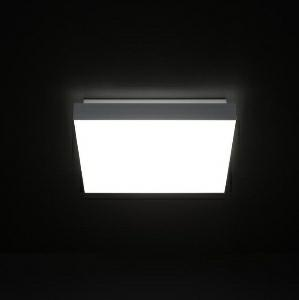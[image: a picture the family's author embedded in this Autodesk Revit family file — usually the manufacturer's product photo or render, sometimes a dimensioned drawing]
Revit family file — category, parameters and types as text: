
# Revit family: spectral_norea_norea-qa_625_5200_840_os_b266
name_source: partatom
category: Lighting Fixtures
revit_build: Autodesk Revit 2016 (Build: 20150220_1215(x64)
units: mm (PartAtom-declared; Revit-internal decimal feet)

## family parameters
Cut with Voids When Loaded = No
Host = Face
Light Source = No
Part Type = Normal
Room Calculation Point = No
Round Connector Dimension = Use Diameter
Shared = No

## types (1)
- SPECTRAL NOREA (1 x )
    Apparent Load = 0 VA
    Approval mark = CE
    CIE Flux Codes = 48 78 95 100 66
    Control Gear = Electronic transformer
    Default Elevation = 1800 mm
    Description = SPT0000010
NOREA surface-mounted luminaire

Design:
Square luminaire element comprising an opal acrylic glass panel in a natural anodised aluminium profile frame surround. The frame is suspended at the
metal body. The LED module is formed as a square LED flat board and screwed to the luminaire element. For connection of the luminaire this can be hinged down and fastened with screws at an oblong hole in the powder-coated metal body. The indirect component is ensured by recesses in the top of the metal body. The metal body accommodates the electrical components and electronic ballast. Luminaire with heat-resistant wiring. Homogenous illumination of the light surface. Suitable for ceiling or wall mounting. 
Protection rating IP20, safety class I.

Colour:
Housing - similar to RAL 9016 white silk matt;
Frame - natural anodised
    Height = 95 mm
    Lamp = 1 x
    Lamp count = 1
    Length = 625 mm
    Luminous efficacy = 0 lm/W
    Manufacturer = Ridi
    ModVariant = No
    Model = NOREA-QA 625/5200/840 OS
    Mounting Place = Ceiling
    Mounting Type = Surface mounted
    Number of Poles = 1
    OnlyDefault = Yes
    Power Factor = 1
    Product Name = SPECTRAL NOREA
    Product group = Ceiling mounted luminaire
    ProductGroupID = 3
    Protection Class = Protection class
    Protection Degree = IP 20
    RlxData = <blob elided: 27909 chars, md5=c2036fc8>
    Socket = socket
    Standby Power = 0 W
    System Light Flux = 0 lm
    System Power = 0 W
    Type Image = noreaquad05_-_kopie.jpg
    URL = http://reluxnet.relux.com
    VarID = 1
    Voltage = 0 V
    Weight = 0.00 kg
    Width = 625 mm

## geometry (parser evidence)
native form markers: Blend x4, Sweep x12
no freeform markers — native parametric forms only
